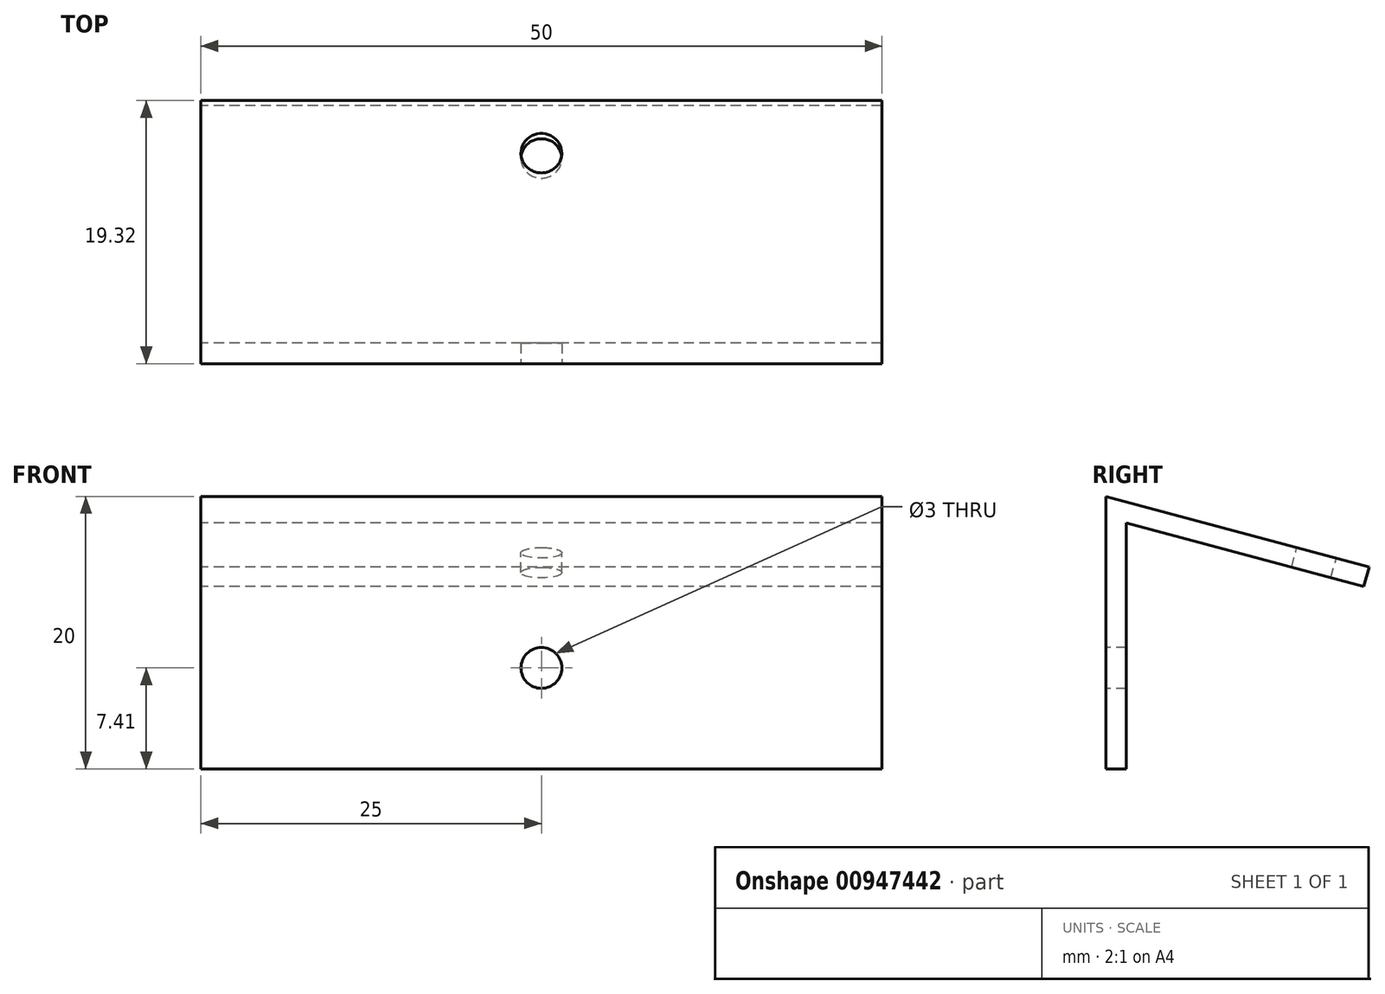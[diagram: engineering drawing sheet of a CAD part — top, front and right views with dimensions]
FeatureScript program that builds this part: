
annotation { "Feature Type Name" : "Feature", "Feature Type Description" : "" }
export const myFeature = defineFeature(function(context is Context, id is Id, definition is map)
    precondition{}
    {
        {
            var Q0;
            Q0=qCreatedBy(makeId("Right.planeOp"),FACE);
            var sketch = newSketch(context, id + "F0", { "sketchPlane" : qUnion([Q0])});
            skLineSegment(sketch, "E0.bottom", {"start": v(-8.16, -7.41) * mm, "end": v(-9.66, -7.41) * mm});
            skLineSegment(sketch, "E0.top", {"start": v(9.66, 7.41) * mm, "end": v(-9.66, 12.59) * mm});
            skLineSegment(sketch, "E0.left", {"start": v(9.27, 5.96) * mm, "end": v(9.66, 7.41) * mm});
            skLineSegment(sketch, "E0.right", {"start": v(-9.66, -7.41) * mm, "end": v(-9.66, 12.59) * mm});
            skPoint(sketch, "E0.middle", {"position": v(0, 0) * mm});
            skLineSegment(sketch, "E1", {"start": v(-8.16, -7.41) * mm, "end": v(-8.16, 10.63) * mm});
            skLineSegment(sketch, "E2", {"start": v(-8.16, 10.63) * mm, "end": v(9.27, 5.96) * mm});
            skPoint(sketch, "E3.orphan", {"position": v(5.69, -7.41) * mm});
            skSolve(sketch);
        }
        {
            var Q0;
            Q0=makeQuery(id+"F0.imprint","IMPRINT",FACE,{"disambiguationData":[TD([[makeQuery(id+"F0.imprint","IMPRINT",EDGE,{"derivedFrom":sQuery(id+"F0.wireOp",EDGE,"E0.bottom")}),-1.0]])]});
            extrude(context, id + "F1", {"entities" : qUnion([Q0]), "depth" : 50 * mm, "offsetDistance" : 25 * mm, "symmetric" : true});
        }
        {
            var Q0;
            Q0=makeQuery(id+"F1.opExtrude","SWEPT_FACE",FACE,{"disambiguationData":[OSD([sQuery(id+"F0.wireOp",EDGE,"E0.right")])]});
            var sketch = newSketch(context, id + "F2", { "sketchPlane" : qUnion([Q0])});
            skCircle(sketch, "E4", {"center": v(0, 0) * mm, "radius": 1.5 * mm});
            skSolve(sketch);
        }
        {
            var Q0;
            Q0=makeQuery(id+"F2.imprint","IMPRINT",FACE,{"disambiguationData":[TD([[makeQuery(id+"F2.imprint","IMPRINT",EDGE,{"derivedFrom":sQuery(id+"F2.wireOp",EDGE,"E4")}),1.0]])]});
            extrude(context, id + "F3", {"entities" : qUnion([Q0]), "operationType" : NewBodyOperationType.REMOVE, "endBound" : BoundingType.UP_TO_NEXT, "oppositeDirection" : true, "depth" : 25 * mm, "offsetDistance" : 25 * mm});
        }
        {
            var Q0;
            Q0=makeQuery(id+"F1.opExtrude","SWEPT_FACE",FACE,{"disambiguationData":[OSD([sQuery(id+"F0.wireOp",EDGE,"E0.top")])]});
            var sketch = newSketch(context, id + "F4", { "sketchPlane" : qUnion([Q0])});
            skCircle(sketch, "E5", {"center": v(0, 3.41) * mm, "radius": 1.5 * mm});
            skPoint(sketch, "E5.centerSnap0", {"position": v(0, 7.41) * mm});
            skSolve(sketch);
        }
        {
            var Q0;
            Q0=makeQuery(id+"F4.imprint","IMPRINT",FACE,{"disambiguationData":[TD([[makeQuery(id+"F4.imprint","IMPRINT",EDGE,{"derivedFrom":sQuery(id+"F4.wireOp",EDGE,"E5")}),1.0]])]});
            extrude(context, id + "F5", {"entities" : qUnion([Q0]), "operationType" : NewBodyOperationType.REMOVE, "endBound" : BoundingType.UP_TO_NEXT, "oppositeDirection" : true, "depth" : 25 * mm, "offsetDistance" : 25 * mm});
        }
    });
